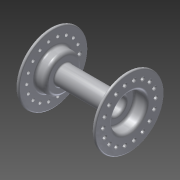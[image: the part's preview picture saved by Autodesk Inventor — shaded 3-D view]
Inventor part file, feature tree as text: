
AUTODESK INVENTOR PART (.ipt)
format: ipt  version: 2015 (Build 190159000, 159)  size: 398,336 bytes
history: native  units: mm
features: other x2, chamfer x2, sketch x2, hole x1, pattern_circular x1
ambient origin geometry x8: Origin, YZ Plane, XZ Plane, XY Plane, X Axis, Y Axis, Z Axis, Center Point
bodies: Body1 (feature_tree)
feature tree (8):
  other  "Bryła1"
  other  "Piasta"
  hole  "Otwór na szprychę"  [1 undecoded]
  chamfer  "Faza1"  Distance=1.0mm
  chamfer  "Faza2"  Angle=90.0deg  [1 undecoded]
  pattern_circular  "Szyk otworów na szprychy"  [2 undecoded]
  sketch  "Szkic1"
  sketch  "Szkic2"
note: 4 required parameter values undecoded (feature->parameter linkage not recoverable at this tier; creation-order binding heuristic only, values carry confidence <= 0.55)
